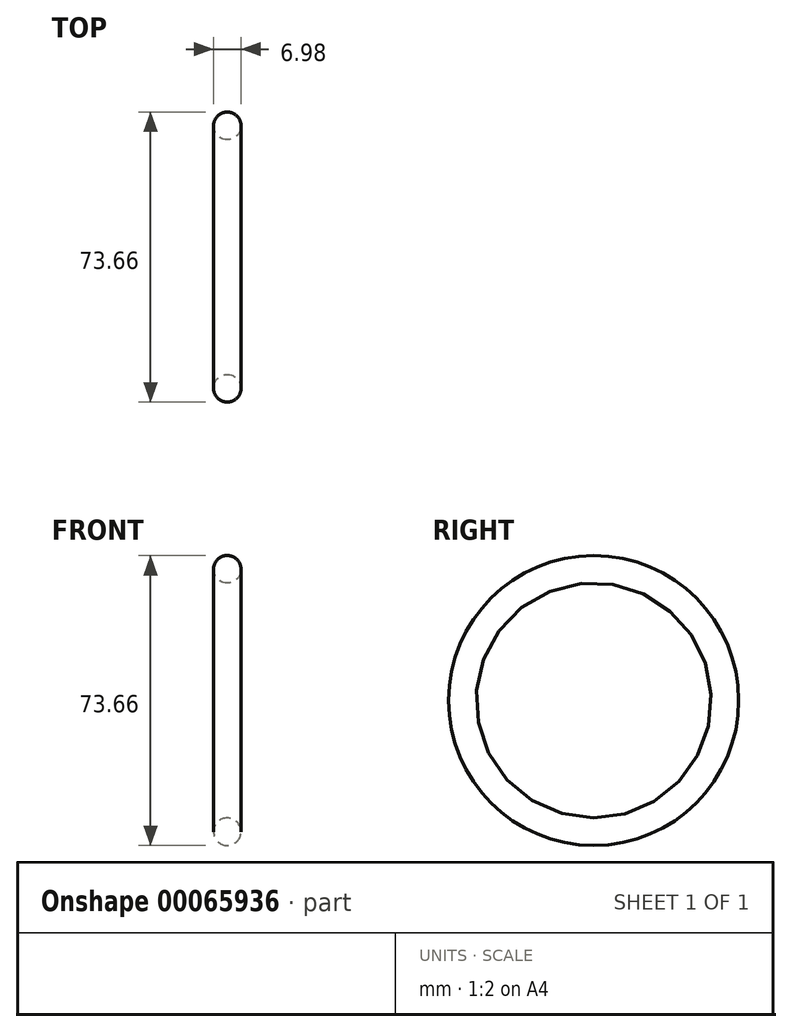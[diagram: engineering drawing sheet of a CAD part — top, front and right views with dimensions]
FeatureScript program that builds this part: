
annotation { "Feature Type Name" : "Feature", "Feature Type Description" : "" }
export const myFeature = defineFeature(function(context is Context, id is Id, definition is map)
    precondition{}
    {
        {
            var Q0;
            Q0=qCreatedBy(makeId("Front.planeOp"),FACE);
            var sketch = newSketch(context, id + "F0", { "sketchPlane" : qUnion([Q0])});
            skLineSegment(sketch, "E0", {"start": v(0, 0) * mm, "end": v(-6.06, 0) * mm, "construction": true});
            skCircle(sketch, "E1", {"center": v(0, 33.34) * mm, "radius": 3.5 * mm});
            skSolve(sketch);
        }
        {
            var Q0;
            Q0=makeQuery(id+"F0.imprint","IMPRINT",FACE,{"disambiguationData":[TD([[makeQuery(id+"F0.imprint","IMPRINT",EDGE,{"derivedFrom":sQuery(id+"F0.wireOp",EDGE,"E1")}),1.0]])]});
            var Q1;
            Q1=sQuery(id+"F0.wireOp",EDGE,"E0");
            revolve(context, id + "F1", {"entities" : qUnion([Q0]), "axis" : qUnion([Q1]), "revolveType" : RevolveType.FULL});
        }
    });
